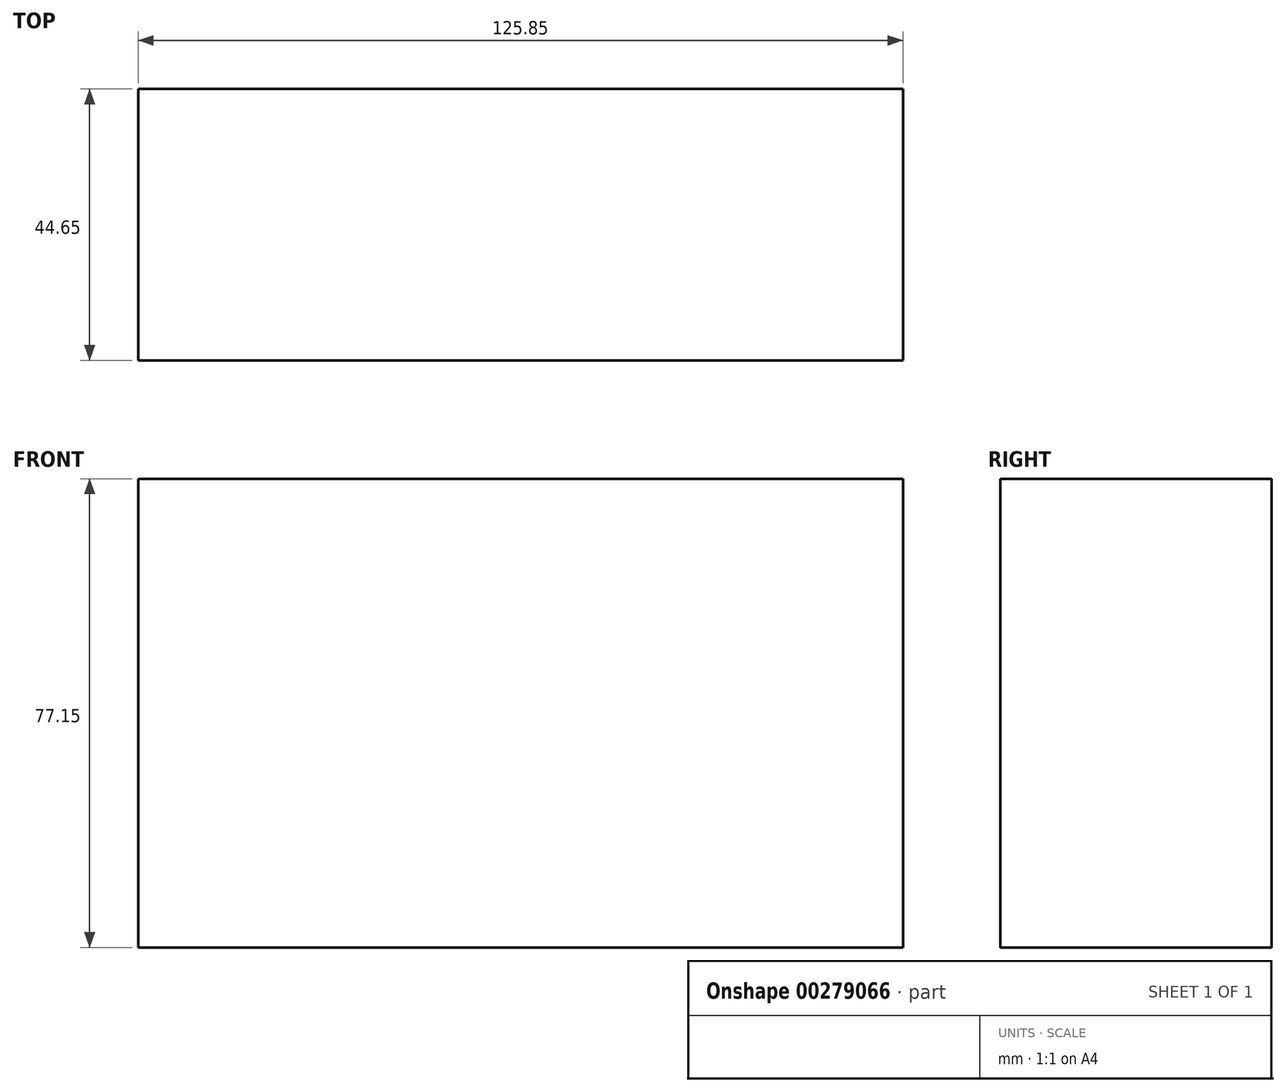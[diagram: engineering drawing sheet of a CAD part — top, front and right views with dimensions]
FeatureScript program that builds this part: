
annotation { "Feature Type Name" : "Feature", "Feature Type Description" : "" }
export const myFeature = defineFeature(function(context is Context, id is Id, definition is map)
    precondition{}
    {
        {
            var Q0;
            Q0=qCreatedBy(makeId("Front.planeOp"),FACE);
            var sketch = newSketch(context, id + "F0", { "sketchPlane" : qUnion([Q0])});
            skLineSegment(sketch, "E0.bottom", {"start": v(-41.54, 38.34) * mm, "end": v(30.05, 38.34) * mm});
            skLineSegment(sketch, "E0.top", {"start": v(-41.54, 15.45) * mm, "end": v(30.05, 15.45) * mm});
            skLineSegment(sketch, "E0.left", {"start": v(-41.54, 38.34) * mm, "end": v(-41.54, 15.45) * mm});
            skLineSegment(sketch, "E0.right", {"start": v(30.05, 38.34) * mm, "end": v(30.05, 15.45) * mm});
            skSolve(sketch);
        }
        {
            var Q0;
            Q0=qCreatedBy(makeId("Front.planeOp"),FACE);
            var sketch = newSketch(context, id + "F1", { "sketchPlane" : qUnion([Q0])});
            skLineSegment(sketch, "E1.0", {"start": v(-68.67, -11.68) * mm, "end": v(57.18, -11.68) * mm});
            skLineSegment(sketch, "E1.1", {"start": v(-68.67, 65.47) * mm, "end": v(-68.67, -11.68) * mm});
            skLineSegment(sketch, "E1.2", {"start": v(-68.67, 65.47) * mm, "end": v(57.18, 65.47) * mm});
            skLineSegment(sketch, "E1.3", {"start": v(57.18, 65.47) * mm, "end": v(57.18, -11.68) * mm});
            skSolve(sketch);
        }
        {
            var Q0;
            Q0=makeQuery(id+"F1.imprint","IMPRINT",FACE,{"disambiguationData":[TD([[makeQuery(id+"F1.imprint","IMPRINT",EDGE,{"derivedFrom":sQuery(id+"F1.wireOp",EDGE,"E1.0")}),1.0]])]});
            var sketch = newSketch(context, id + "F4", { "sketchPlane" : qUnion([Q0])});
            skSolve(sketch);
        }
        {
            var Q0;
            Q0=makeQuery(id+"F1.imprint","IMPRINT",FACE,{"disambiguationData":[TD([[makeQuery(id+"F1.imprint","IMPRINT",EDGE,{"derivedFrom":sQuery(id+"F1.wireOp",EDGE,"E1.0")}),1.0]])]});
            extrude(context, id + "F2", {"entities" : qUnion([Q0]), "depth" : 25.4 * mm});
        }
        {
            var Q0;
            Q0=makeQuery(id+"F4.imprint","IMPRINT",FACE,{"disambiguationData":[TD([[makeQuery(id+"F4.imprint","IMPRINT",EDGE,{"derivedFrom":makeQuery(id+"F1.imprint","IMPRINT",EDGE,{"derivedFrom":sQuery(id+"F1.wireOp",EDGE,"E1.0")})}),1.0]])]});
            var sketch = newSketch(context, id + "F5", { "sketchPlane" : qUnion([Q0])});
            skSolve(sketch);
        }
        {
            var Q0;
            Q0=makeQuery(id+"F5.imprint","IMPRINT",FACE,{"disambiguationData":[TD([[makeQuery(id+"F5.imprint","IMPRINT",EDGE,{"derivedFrom":makeQuery(id+"F4.imprint","IMPRINT",EDGE,{"derivedFrom":makeQuery(id+"F1.imprint","IMPRINT",EDGE,{"derivedFrom":sQuery(id+"F1.wireOp",EDGE,"E1.0")})})}),1.0]])]});
            var Q1;
            Q1=makeQuery(id+"F0.imprint","IMPRINT",FACE,{"disambiguationData":[TD([[makeQuery(id+"F0.imprint","IMPRINT",EDGE,{"derivedFrom":sQuery(id+"F0.wireOp",EDGE,"E0.bottom")}),-1.0]])]});
            extrude(context, id + "F3", {"entities" : qUnion([Q0, Q1]), "operationType" : NewBodyOperationType.ADD, "depth" : 44.65 * mm});
        }
    });
